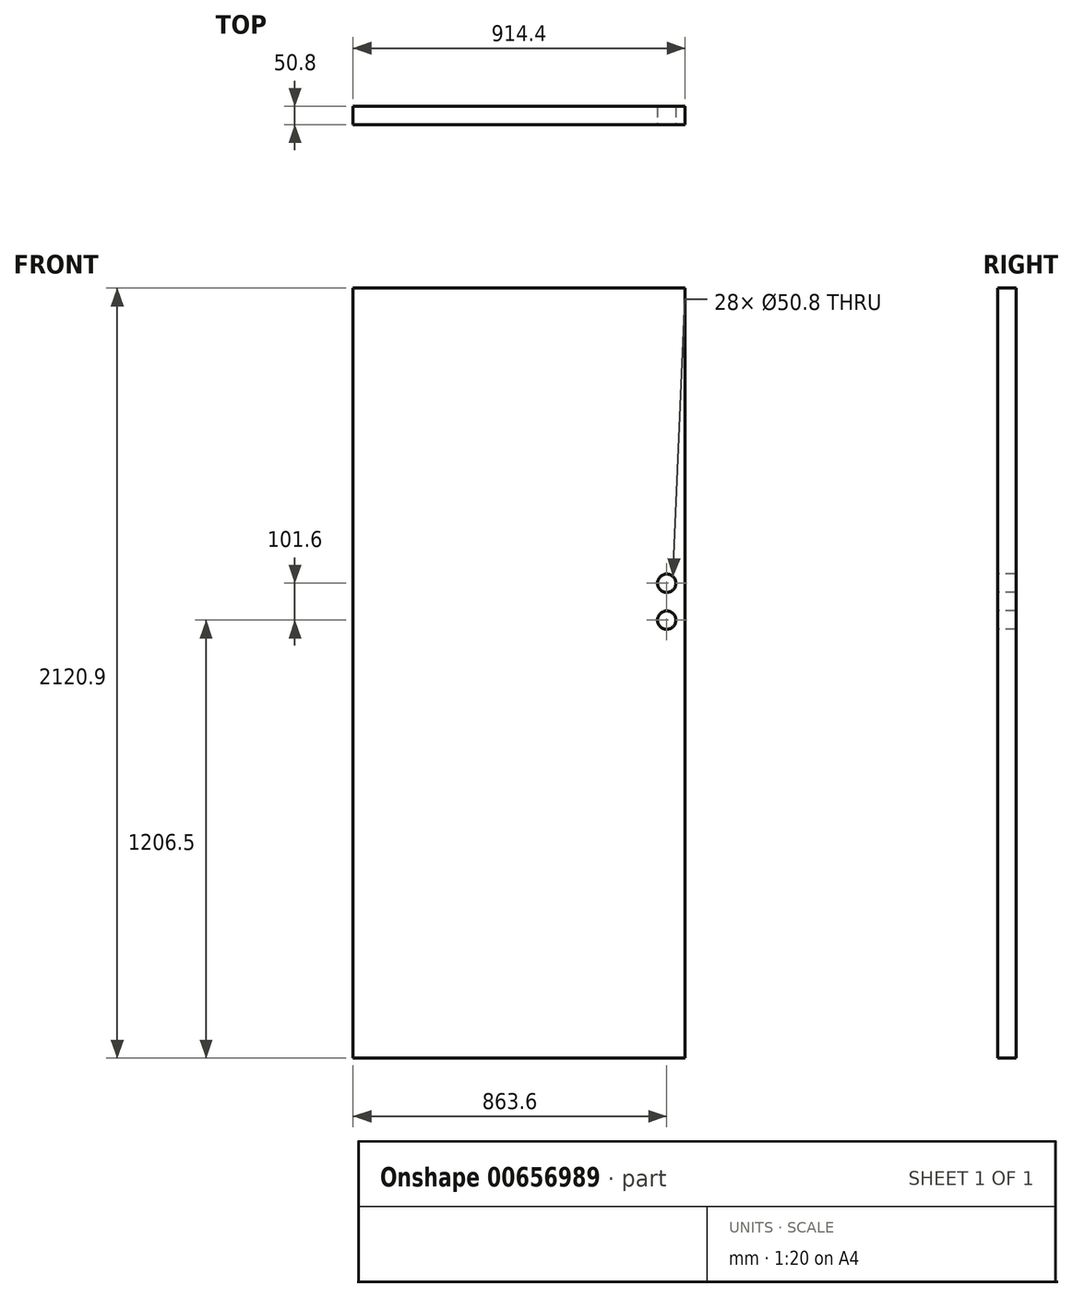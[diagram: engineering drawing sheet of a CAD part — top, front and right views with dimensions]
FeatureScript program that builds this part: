
annotation { "Feature Type Name" : "Feature", "Feature Type Description" : "" }
export const myFeature = defineFeature(function(context is Context, id is Id, definition is map)
    precondition{}
    {
        {
            var Q0;
            Q0=qCreatedBy(makeId("Front.planeOp"),FACE);
            var sketch = newSketch(context, id + "F0", { "sketchPlane" : qUnion([Q0])});
            skLineSegment(sketch, "E0.bottom", {"start": v(-457.2, 1060.45) * mm, "end": v(457.2, 1060.45) * mm});
            skLineSegment(sketch, "E0.top", {"start": v(-457.2, -1060.45) * mm, "end": v(457.2, -1060.45) * mm});
            skLineSegment(sketch, "E0.left", {"start": v(-457.2, 1060.45) * mm, "end": v(-457.2, -1060.45) * mm});
            skLineSegment(sketch, "E0.right", {"start": v(457.2, 1060.45) * mm, "end": v(457.2, -1060.45) * mm});
            skSolve(sketch);
        }
        {
            var Q0;
            Q0 = qSketchRegion(id + "F0", true);
            extrude(context, id + "F1", {"entities" : qUnion([Q0]), "depth" : 50.8 * mm, "offsetDistance" : 25.4 * mm});
        }
        {
            var Q0;
            Q0=makeQuery(id+"F1.opExtrude","CAP_FACE",FACE,{"disambiguationData":[OSD([sQuery(id+"F0.wireOp",EDGE,"E0.bottom"),sQuery(id+"F0.wireOp",EDGE,"E0.top"),sQuery(id+"F0.wireOp",EDGE,"E0.left"),sQuery(id+"F0.wireOp",EDGE,"E0.right")])],"isStart":false});
            var sketch = newSketch(context, id + "F2", { "sketchPlane" : qUnion([Q0])});
            skCircle(sketch, "E1", {"center": v(406.4, 247.65) * mm, "radius": 25.4 * mm});
            skCircle(sketch, "E2", {"center": v(406.4, 146.05) * mm, "radius": 25.4 * mm});
            skSolve(sketch);
        }
        {
            var Q0;
            Q0 = qSketchRegion(id + "F2", true);
            extrude(context, id + "F3", {"entities" : qUnion([Q0]), "operationType" : NewBodyOperationType.REMOVE, "endBound" : BoundingType.THROUGH_ALL, "oppositeDirection" : true, "depth" : 25.4 * mm, "offsetDistance" : 25.4 * mm});
        }
    });
